# Revit family: Rheem Indoor Stainless Steel HWC
name_source: partatom
category: Plumbing Fixtures
units: mm (PartAtom-declared; Revit-internal decimal feet)

## family parameters
Always vertical = Yes
Cut with Voids When Loaded = No
Enable Cutting in Views = No
Maintain Annotation Orientation = No
OmniClass Number = 23.45.00.00
OmniClass Title = Sanitary, Laundry, and Cleaning Equipment
Part Type = Normal
Room Calculation Point = No
Round Connector Dimension = Use Diameter
Shared = No
Work Plane-Based = No

## types (6) — shared parameters
A - Cylinder Diameter = 560 mm  [stored 1.83727 ft]
CW Connection = Yes
Domestic Warranty = 10 years
Electrical Connection = 230V AC 50Hz
Element Type = INC800 Screw In
F - Lower Element = 1 1/4 Inch BSP F
HW Connection = Yes
Inlet & Outlet Size = 20 mm  [stored 0.0656168 ft]
Installation Location = Indoor
Manufacturer = Rheem
Material = Stainless Steel
T&PR Connection Size = 20 mm  [stored 0.0656168 ft]
Thermostat Setting Max = 70 °C
Thermostat Setting Min = 60 °C
URL = https://rheem.co.nz
Vent Connection = Yes
Waste Connection = No
zero-valued in all types: Default Elevation

## per-type parameters (varying)
| type | # People (Cold Climate) | # People (Moderate Climate) | B - Hot Water Draw-Off (Height) | C D - Cold Feeds | E - Safety TPR | Model | Rating | Storage Capacity | Type Comments | Weight Empty Approx. |
| 135L 2kW | 1 to 2 | 1 to 3 | 1010 mm  [stored 3.31365 ft] | 195 mm  [stored 0.639764 ft] | 790 mm  [stored 2.59186 ft] | 3553513 | 2000 W | 135 m³ | Indoor Stainless Steel HWC 135L | 28.00 kg |
| 135L 3kW | 1 to 2 | 1 to 3 | 1010 mm  [stored 3.31365 ft] | 195 mm  [stored 0.639764 ft] | 790 mm  [stored 2.59186 ft] | 3553515 | 3000 W | 135 m³ | Indoor Stainless Steel HWC 135L | 28.00 kg |
| 180L 2kW | 3 to 4 | 3 to 5 | 1295 mm | 195 mm  [stored 0.639764 ft] | 1075 mm | 35518013 | 2000 W | 135 m³ | Indoor Stainless Steel HWC 180L | 36.00 kg |
| 180L 3kW | 3 to 4 | 3 to 5 | 1295 mm | 195 mm  [stored 0.639764 ft] | 1075 mm | 35518015 | 3000 W | 180 m³ | Indoor Stainless Steel HWC 180L | 36.00 kg |
| 250L 3kW | 3 to 5 | 3 to 6 | 1730 mm  [stored 5.67585 ft] | 185 mm  [stored 0.606955 ft] | 1510 mm  [stored 4.95407 ft] | 35525015 | 3000 W | 250 m³ | Indoor Stainless Steel HWC 250L | 46.00 kg |
| 300L 3kW | 3 to 5 | 3 to 6 | 2045 mm  [stored 6.70932 ft] | 185 mm  [stored 0.606955 ft] | 1825 mm  [stored 5.98753 ft] | 35530015 | 3000 W | 300 m³ | Indoor Stainless Steel HWC 300L | 51.00 kg |

note: [stored X ft] marks values corroborated as IEEE doubles in the binary element streams (Revit-internal decimal feet)

## geometry (parser evidence)
native form markers: Sweep x2
no freeform markers — native parametric forms only
